# Revit family: LUCCIOLA-Floor
name_source: partatom
category: Lighting Fixtures
units: mm (PartAtom-declared; Revit-internal decimal feet)

## family parameters
Always vertical = Yes
Cut with Voids When Loaded = No
Light Source = No
OmniClass Number = 23.80.70.00
OmniClass Title = Lighting
Part Type = Normal
Room Calculation Point = No
Round Connector Dimension = Use Diameter
Shared = No
Work Plane-Based = Yes

## types (2) — shared parameters
Bulb Diametr = 15 mm  [stored 0.0492126 ft]
Country = Europe
Default Elevation = 1219 mm
Description = FLOOR LAMP
Designer = Studio Debonademeo
Height = 1600 mm  [stored 5.24934 ft]
Lampshad Type = LUCCIOLA_Lampshade : LUCCISP M and LUCCIOLA PP M
Manufacturer = Vistosi
Manufacturer country = Italy
Model = LUCCIOLA
Type Comments = Studio Debonademeo
URL = https://vistosi.com
URL Product Page = https://vistosi.it
Width = 28 mm
zero-valued in all types: Depth

## type names (no varying parameters)
- LUCCIOLA PT P
- LUCCIOLA PT M

note: [stored X ft] marks values corroborated as IEEE doubles in the binary element streams (Revit-internal decimal feet)

## geometry (parser evidence)
native form markers: Sweep x6
no freeform markers — native parametric forms only
